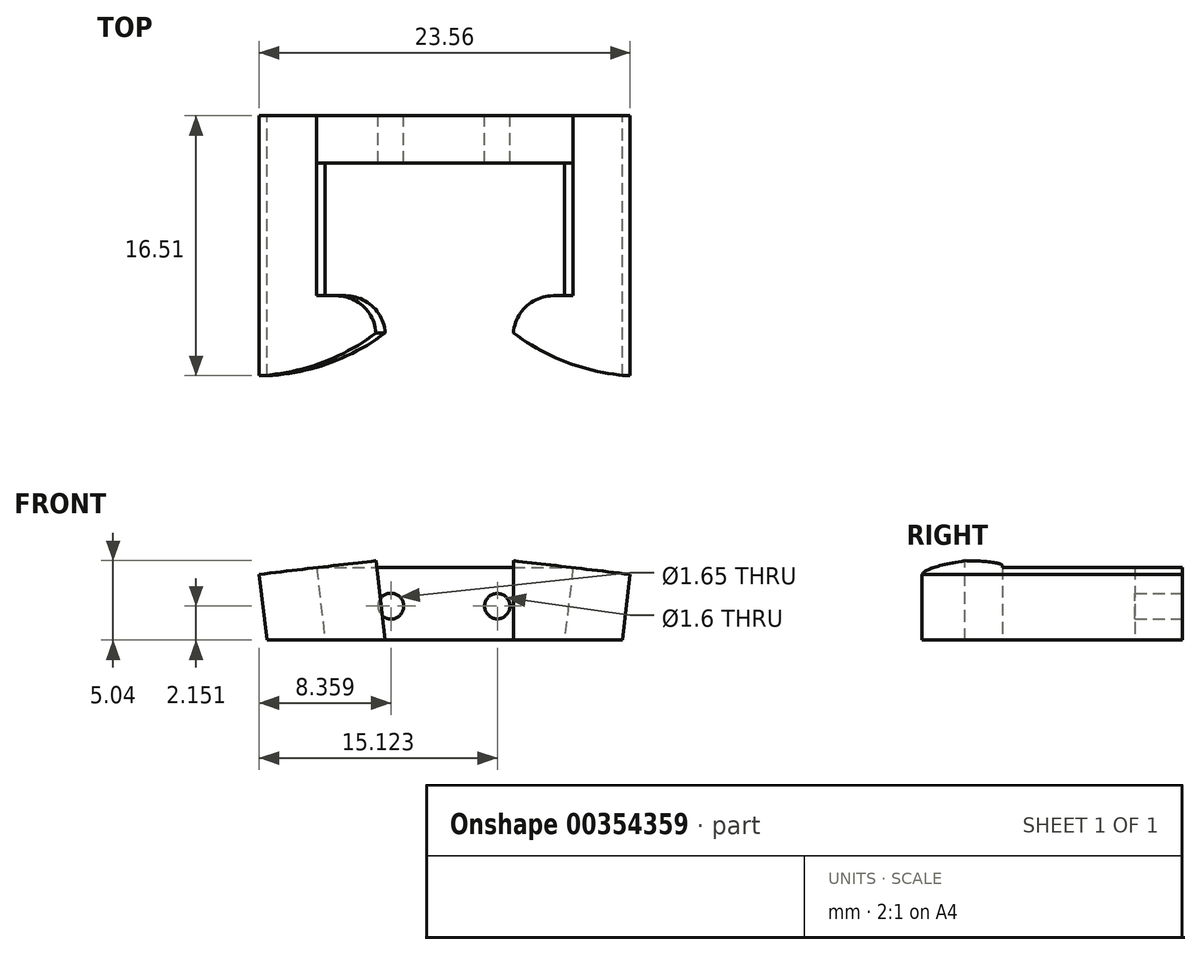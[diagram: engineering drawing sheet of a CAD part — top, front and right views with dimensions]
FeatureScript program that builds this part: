
annotation { "Feature Type Name" : "Feature", "Feature Type Description" : "" }
export const myFeature = defineFeature(function(context is Context, id is Id, definition is map)
    precondition{}
    {
        {
            var Q0;
            Q0=qCreatedBy(makeId("Front.planeOp"),FACE);
            var sketch = newSketch(context, id + "F0", { "sketchPlane" : qUnion([Q0])});
            skLineSegment(sketch, "E0", {"start": v(-9.32, 10.76) * mm, "end": v(6.96, 10.76) * mm});
            skLineSegment(sketch, "E1", {"start": v(-8.78, 6.16) * mm, "end": v(6.43, 6.16) * mm});
            skLineSegment(sketch, "E2", {"start": v(-9.32, 10.76) * mm, "end": v(-8.78, 6.16) * mm});
            skLineSegment(sketch, "E3", {"start": v(6.96, 10.76) * mm, "end": v(6.43, 6.16) * mm});
            skLineSegment(sketch, "E4", {"start": v(-9.32, 10.76) * mm, "end": v(-12.96, 10.33) * mm});
            skLineSegment(sketch, "E5", {"start": v(-8.78, 6.16) * mm, "end": v(-12.47, 6.16) * mm});
            skLineSegment(sketch, "E6", {"start": v(-12.96, 10.33) * mm, "end": v(-12.47, 6.16) * mm});
            skCircle(sketch, "E7", {"center": v(-4.6, 8.31) * mm, "radius": 0.82 * mm});
            skCircle(sketch, "E8", {"center": v(2.16, 8.31) * mm, "radius": 0.8 * mm});
            skLineSegment(sketch, "E9", {"start": v(6.96, 10.76) * mm, "end": v(10.6, 10.33) * mm});
            skLineSegment(sketch, "E10", {"start": v(10.6, 10.33) * mm, "end": v(10.11, 6.16) * mm});
            skLineSegment(sketch, "E11", {"start": v(10.11, 6.16) * mm, "end": v(6.43, 6.16) * mm});
            skSolve(sketch);
        }
        {
            var Q0;
            Q0=makeQuery(id+"F0.imprint","IMPRINT",FACE,{"disambiguationData":[TD([[makeQuery(id+"F0.imprint","IMPRINT",EDGE,{"derivedFrom":sQuery(id+"F0.wireOp",EDGE,"E0")}),-1.0]])]});
            extrude(context, id + "F1", {"entities" : qUnion([Q0]), "depth" : 3 * mm});
        }
        {
            var Q0;
            Q0=makeQuery(id+"F0.imprint","IMPRINT",FACE,{"disambiguationData":[TD([[makeQuery(id+"F0.imprint","IMPRINT",EDGE,{"derivedFrom":sQuery(id+"F0.wireOp",EDGE,"E2")}),-1.0]])]});
            var Q1;
            Q1=makeQuery(id+"F0.imprint","IMPRINT",FACE,{"disambiguationData":[TD([[makeQuery(id+"F0.imprint","IMPRINT",EDGE,{"derivedFrom":sQuery(id+"F0.wireOp",EDGE,"E3")}),1.0]])]});
            extrude(context, id + "F2", {"entities" : qUnion([Q0, Q1]), "operationType" : NewBodyOperationType.ADD, "depth" : 11.43 * mm});
        }
        {
            var Q0;
            Q0=makeQuery(id+"F2.opExtrude","CAP_FACE",FACE,{"disambiguationData":[OSD([sQuery(id+"F0.wireOp",EDGE,"E2"),sQuery(id+"F0.wireOp",EDGE,"E4"),sQuery(id+"F0.wireOp",EDGE,"E5"),sQuery(id+"F0.wireOp",EDGE,"E6")])],"isStart":false});
            var sketch = newSketch(context, id + "F3", { "sketchPlane" : qUnion([Q0])});
            skLineSegment(sketch, "E12", {"start": v(-9.32, 10.76) * mm, "end": v(-5.54, 11.2) * mm});
            skLineSegment(sketch, "E13", {"start": v(-5.54, 11.2) * mm, "end": v(-4.94, 6.16) * mm});
            skLineSegment(sketch, "E14", {"start": v(-4.94, 6.16) * mm, "end": v(-8.78, 6.16) * mm});
            skSolve(sketch);
        }
        {
            var Q0;
            Q0=makeQuery(id+"F2.opExtrude","CAP_FACE",FACE,{"disambiguationData":[OSD([sQuery(id+"F0.wireOp",EDGE,"E3"),sQuery(id+"F0.wireOp",EDGE,"E9"),sQuery(id+"F0.wireOp",EDGE,"E10"),sQuery(id+"F0.wireOp",EDGE,"E11")])],"isStart":false});
            var sketch = newSketch(context, id + "F4", { "sketchPlane" : qUnion([Q0])});
            skLineSegment(sketch, "E15", {"start": v(6.96, 10.76) * mm, "end": v(3.18, 11.2) * mm});
            skLineSegment(sketch, "E16", {"start": v(3.18, 11.2) * mm, "end": v(3.18, 6.16) * mm});
            skLineSegment(sketch, "E17", {"start": v(3.18, 6.16) * mm, "end": v(6.43, 6.16) * mm});
            skSolve(sketch);
        }
        {
            var Q0;
            Q0=makeQuery(id+"F3.imprint","IMPRINT",FACE,{"disambiguationData":[TD([[makeQuery(id+"F3.imprint","IMPRINT",EDGE,{"derivedFrom":sQuery(id+"F3.wireOp",EDGE,"E12")}),-1.0]])]});
            var Q1;
            Q1=makeQuery(id+"F3.imprint","IMPRINT",FACE,{"disambiguationData":[TD([[makeQuery(id+"F3.imprint","IMPRINT",EDGE,{"derivedFrom":makeQuery(id+"F2.opExtrude","CAP_EDGE",EDGE,{"disambiguationData":[OSD([sQuery(id+"F0.wireOp",EDGE,"E2")])],"isStart":false})}),-1.0]])]});
            var Q2;
            Q2=makeQuery(id+"F4.imprint","IMPRINT",FACE,{"disambiguationData":[TD([[makeQuery(id+"F4.imprint","IMPRINT",EDGE,{"derivedFrom":sQuery(id+"F4.wireOp",EDGE,"E15")}),1.0]])]});
            var Q3;
            Q3=makeQuery(id+"F4.imprint","IMPRINT",FACE,{"disambiguationData":[TD([[makeQuery(id+"F4.imprint","IMPRINT",EDGE,{"derivedFrom":makeQuery(id+"F2.opExtrude","CAP_EDGE",EDGE,{"disambiguationData":[OSD([sQuery(id+"F0.wireOp",EDGE,"E3")])],"isStart":false})}),1.0]])]});
            extrude(context, id + "F5", {"entities" : qUnion([Q0, Q1, Q2, Q3]), "operationType" : NewBodyOperationType.ADD, "depth" : 5.08 * mm});
        }
        {
            var Q0;
            Q0=makeQuery(id+"F5.opExtrude","CAP_EDGE",EDGE,{"disambiguationData":[OSD([sQuery(id+"F4.wireOp",EDGE,"E16")])],"isStart":true});
            var Q1;
            Q1=makeQuery(id+"F5.opExtrude","CAP_EDGE",EDGE,{"disambiguationData":[OSD([sQuery(id+"F3.wireOp",EDGE,"E13")])],"isStart":true});
            fillet(context, id + "F6", {"entities" : qUnion([Q0, Q1]), "radius" : 2.54 * mm, "tangentPropagation" : true, "allowEdgeOverflow" : false});
        }
        {
            var Q0;
            Q0=makeQuery(id+"F5.opExtrude","CAP_EDGE",EDGE,{"disambiguationData":[OSD([sQuery(id+"F3.wireOp",EDGE,"E13")])],"isStart":false});
            var Q1;
            Q1=makeQuery(id+"F5.opExtrude","CAP_EDGE",EDGE,{"disambiguationData":[OSD([sQuery(id+"F4.wireOp",EDGE,"E16")])],"isStart":false});
            chamfer(context, id + "F7", {"entities" : qUnion([Q0, Q1]), "width" : 2.54 * mm, "tangentPropagation" : true});
        }
        {
            var Q0;
            {var subQ0=sQuery(id+"F4.wireOp",EDGE,"E16");Q0=makeQuery(id+"F7.opChamfer","BLEND_EDGE",EDGE,{"blendedFrom":[makeQuery(id+"F5.opExtrude","CAP_EDGE",EDGE,{"disambiguationData":[OSD([subQ0])],"isStart":false}),makeQuery(id+"F5.opExtrude","CAP_FACE",FACE,{"disambiguationData":[OSD([sQuery(id+"F0.wireOp",EDGE,"E9"),sQuery(id+"F0.wireOp",EDGE,"E10"),sQuery(id+"F0.wireOp",EDGE,"E11"),sQuery(id+"F4.wireOp",EDGE,"E15"),subQ0,sQuery(id+"F4.wireOp",EDGE,"E17")])],"isStart":false})],"blendedInto":[makeQuery(id+"F5.opExtrude","CAP_FACE",FACE,{"disambiguationData":[OSD([sQuery(id+"F0.wireOp",EDGE,"E9"),sQuery(id+"F0.wireOp",EDGE,"E10"),sQuery(id+"F0.wireOp",EDGE,"E11"),sQuery(id+"F4.wireOp",EDGE,"E15"),subQ0,sQuery(id+"F4.wireOp",EDGE,"E17")])],"isStart":false})]});}
            var Q1;
            {var subQ0=sQuery(id+"F3.wireOp",EDGE,"E13");Q1=makeQuery(id+"F7.opChamfer","BLEND_EDGE",EDGE,{"blendedFrom":[makeQuery(id+"F5.opExtrude","CAP_EDGE",EDGE,{"disambiguationData":[OSD([subQ0])],"isStart":false}),makeQuery(id+"F5.opExtrude","CAP_FACE",FACE,{"disambiguationData":[OSD([sQuery(id+"F0.wireOp",EDGE,"E4"),sQuery(id+"F0.wireOp",EDGE,"E5"),sQuery(id+"F0.wireOp",EDGE,"E6"),sQuery(id+"F3.wireOp",EDGE,"E12"),subQ0,sQuery(id+"F3.wireOp",EDGE,"E14")])],"isStart":false})],"blendedInto":[makeQuery(id+"F5.opExtrude","CAP_FACE",FACE,{"disambiguationData":[OSD([sQuery(id+"F0.wireOp",EDGE,"E4"),sQuery(id+"F0.wireOp",EDGE,"E5"),sQuery(id+"F0.wireOp",EDGE,"E6"),sQuery(id+"F3.wireOp",EDGE,"E12"),subQ0,sQuery(id+"F3.wireOp",EDGE,"E14")])],"isStart":false})]});}
            fillet(context, id + "F8", {"entities" : qUnion([Q0, Q1]), "radius" : 13.56 * mm, "tangentPropagation" : true, "allowEdgeOverflow" : false});
        }
    });
